# Revit family: ef_eg-25_40asxc2_bsxc2_dsxc2_csxc2-hc_50Hz
name_source: partatom
category: 機械設備
units: mm (PartAtom-declared; Revit-internal decimal feet)

## family parameters
OmniClass タイトル = Industrial Ventilating Equipment
OmniClass 番号 = 23.75.35.21.17
パーツ タイプ = 標準
ロード時にボイドで切り取り = はい
丸型コネクタ寸法 = 直径を使用
作業面ベース = いいえ
共有 = いいえ
常に垂直 = はい
部屋計算ポイント = はい

## types (4) — shared parameters
IfcExportAs = IfcFanType
IfcExportType = TUBEAXIAL
MID風量 = 0.0 m³/h
MIN風量 = 0.0 m³/h
OmniClassCode = 23-33 31 19 11 17
URL = https://www.mitsubishielectric.co.jp
Uniclass2015Code = Pr_65_67_29_67
Uniclass2015Title = Propeller fans
Uniclass2015Version = Systems v1.9
ファンの種類 = 軸流羽根
フレームの厚さ = 10  [stored 0.0328084 ft]
仕様書バージョン = Version1.0
企業コード = 108420
分類コード = 50052503100110
周波数 = 50 Hz
呼称 = 有圧扇
極数 = 2
法定耐用年数 = 15
相 = 1
製品リリース年月 = 2022年6月1日
製品出荷対象 = 国内
製造元 = 三菱電機株式会社
設置方法 = 壁付
説明 = 産業用有圧換気扇 低騒音形ステンレスタイプ オールステンレス厨房用
負荷分類 = 3_ファン類
運転質量 = 0.00 kg
電圧 = 100 V

## per-type parameters (varying)
| type | Box_H | Box_W | Depth | Height | MAX風量 | Width | オリフィス径 | ボックス_Depth | ボックス_Height | ボックス_Width | モーター径 | レグ_Depth | 価格 | 極 | 消費電力 | 羽根径 | 製品質量 | 質量 | 電動機出力 |
| EF-25ASXC2-HC | 83 | 137  [stored 0.449475 ft] | 164  [stored 0.538058 ft] | 370  [stored 1.21391 ft] | 1080.0 m³/h | 370  [stored 1.21391 ft] | 298  [stored 0.97769 ft] | 45 | 131  [stored 0.42979 ft] | 46 | 99  [stored 0.324803 ft] | 148 | 181000 $ | 4 | 50 W | ∅250 | 4.40 kg | 5.28 kg | 25 W |
| EF-30BSXC2-HC | 108 | 162  [stored 0.531496 ft] | 164  [stored 0.538058 ft] | 420  [stored 1.37795 ft] | 1680.0 m³/h | 420  [stored 1.37795 ft] | 348  [stored 1.14173 ft] | 45 | 191 | 46 | 99  [stored 0.324803 ft] | 148 | 244000 $ | 4 | 60 W | ∅300 | 5.40 kg | 6.48 kg | 50 W |
| EF-40DSXC2-HC | 135 | 213 | 225  [stored 0.738189 ft] | 520  [stored 1.70604 ft] | 3760.0 m³/h | 520  [stored 1.70604 ft] | 476  [stored 1.56168 ft] | 58 | 251 | 47 | 113  [stored 0.370735 ft] | 199 | 304000 $ | 4 | 125 W | ∅400 | 12.50 kg | 15.00 kg | 200 W |
| EG-40CSXC2-HC | 135 | 213 | 249  [stored 0.816929 ft] | 520  [stored 1.70604 ft] | 3060.0 m³/h | 520  [stored 1.70604 ft] | 476  [stored 1.56168 ft] | 58 | 251 | 47 | 113  [stored 0.370735 ft] | 213 | 290000 $ | 6 | 99 W | ∅400 | 12.50 kg | 15.00 kg | 100 W |

note: column(s) folded — value = type name in every type: モデル

note: [stored X ft] marks values corroborated as IEEE doubles in the binary element streams (Revit-internal decimal feet)
